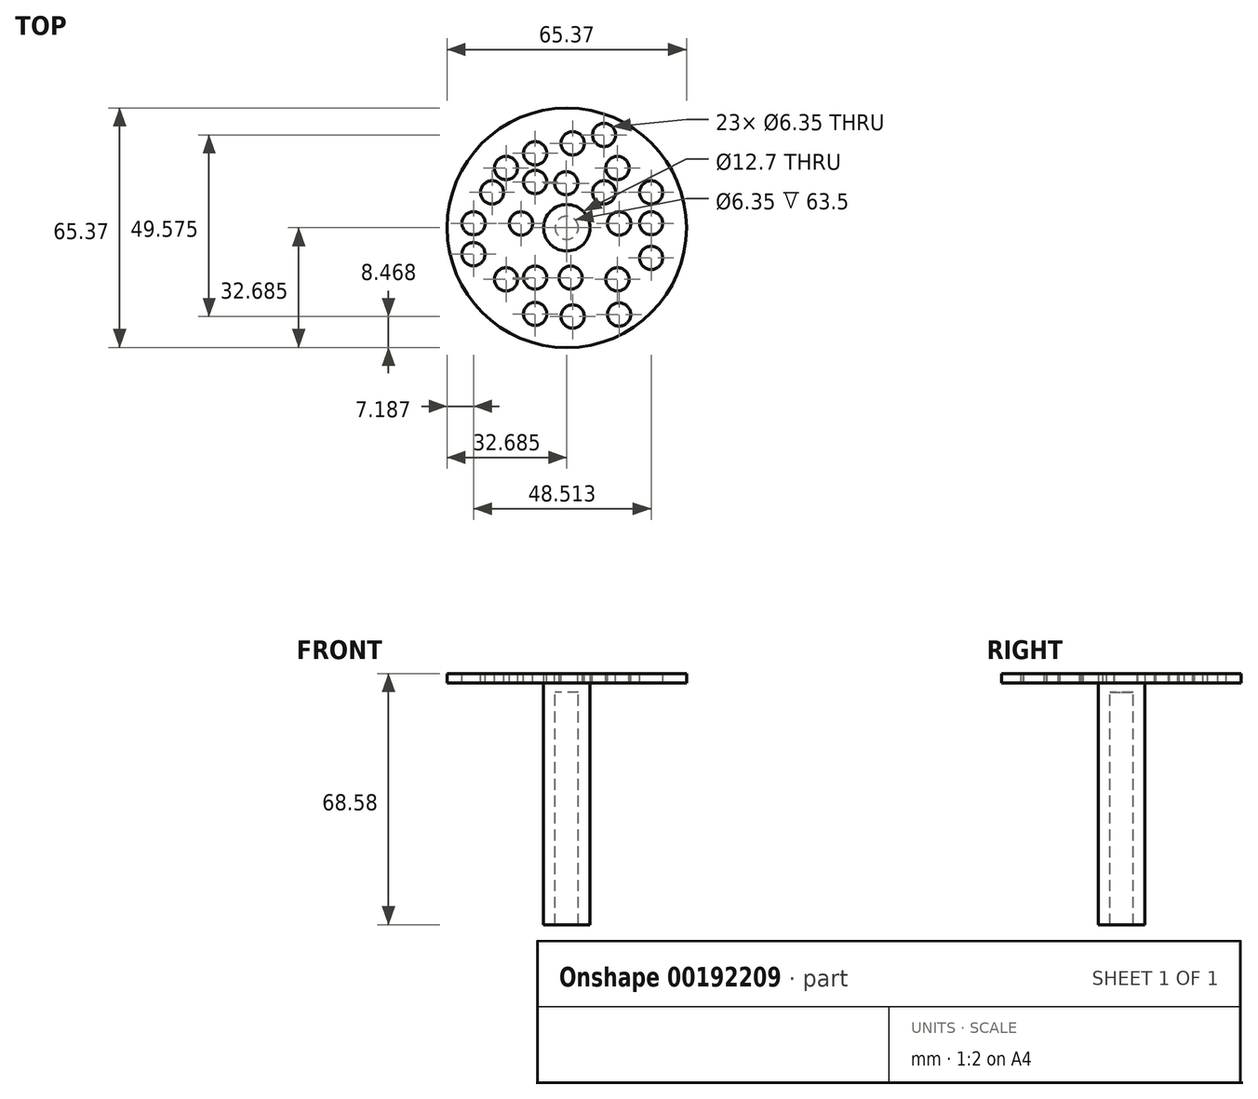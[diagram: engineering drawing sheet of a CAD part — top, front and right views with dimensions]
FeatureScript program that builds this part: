
annotation { "Feature Type Name" : "Feature", "Feature Type Description" : "" }
export const myFeature = defineFeature(function(context is Context, id is Id, definition is map)
    precondition{}
    {
        {
            var Q0;
            Q0=qCreatedBy(makeId("Top.planeOp"),FACE);
            var sketch = newSketch(context, id + "F0", { "sketchPlane" : qUnion([Q0])});
            skCircle(sketch, "E0", {"center": v(-23.02, -49.18) * mm, "radius": 6.35 * mm});
            skSolve(sketch);
        }
        {
            var Q0;
            Q0=makeQuery(id+"F0.imprint","IMPRINT",FACE,{"disambiguationData":[TD([[makeQuery(id+"F0.imprint","IMPRINT",EDGE,{"derivedFrom":sQuery(id+"F0.wireOp",EDGE,"E0")}),1.0]])]});
            extrude(context, id + "F1", {"entities" : qUnion([Q0]), "depth" : 63.5 * mm});
        }
        {
            var Q0;
            Q0=makeQuery(id+"F1.opExtrude","CAP_FACE",FACE,{"disambiguationData":[OSD([sQuery(id+"F0.wireOp",EDGE,"E0")])],"isStart":false});
            var sketch = newSketch(context, id + "F2", { "sketchPlane" : qUnion([Q0])});
            skCircle(sketch, "E1", {"center": v(-23.02, -49.18) * mm, "radius": 6.35 * mm});
            skSolve(sketch);
        }
        {
            var Q0;
            Q0=makeQuery(id+"F1.opExtrude","CAP_FACE",FACE,{"disambiguationData":[OSD([sQuery(id+"F0.wireOp",EDGE,"E0")])],"isStart":false});
            var sketch = newSketch(context, id + "F3", { "sketchPlane" : qUnion([Q0])});
            skSolve(sketch);
        }
        {
            var Q0;
            Q0=qSketchRegion(id+"F3",true);
            var Q1;
            Q1=makeQuery(id+"F3.imprint","IMPRINT",FACE,{"disambiguationData":[TD([[makeQuery(id+"F3.imprint","IMPRINT",EDGE,{"derivedFrom":makeQuery(id+"F1.opExtrude","CAP_EDGE",EDGE,{"disambiguationData":[OSD([sQuery(id+"F0.wireOp",EDGE,"E0")])],"isStart":false})}),1.0]])]});
            extrude(context, id + "F4", {"entities" : qUnion([Q0, Q1]), "operationType" : NewBodyOperationType.ADD, "depth" : 2.54 * mm});
        }
        {
            var Q0;
            Q0=sQuery(id+"F2.wireOp",VERTEX,"E1.center");
            var Q1;
            Q1=makeQuery(id+"F1.opExtrude","SWEPT_BODY",BODY,{"disambiguationData":[OSD([sQuery(id+"F0.wireOp",EDGE,"E0")])]});
            hole(context, id + "F5", {"style" : HoleStyle.SIMPLE, "endStyle" : HoleEndStyle.BLIND, "holeDiameter" : 6.35 * mm, "holeDepth" : 63.5 * mm, "startFromSketch" : true, "locations" : qUnion([Q0]), "scope" : qUnion([Q1])});
        }
        {
            var Q0;
            Q0=makeQuery(id+"F4.opExtrude","CAP_FACE",FACE,{"disambiguationData":[OSD([sQuery(id+"F0.wireOp",EDGE,"E0")])],"isStart":false});
            var sketch = newSketch(context, id + "F6", { "sketchPlane" : qUnion([Q0])});
            skCircle(sketch, "E2", {"center": v(-23.02, -49.18) * mm, "radius": 32.69 * mm});
            skSolve(sketch);
        }
        {
            var Q0;
            Q0=makeQuery(id+"F6.imprint","IMPRINT",FACE,{"disambiguationData":[TD([[makeQuery(id+"F6.imprint","IMPRINT",EDGE,{"derivedFrom":sQuery(id+"F6.wireOp",EDGE,"E2")}),1.0]])]});
            extrude(context, id + "F7", {"entities" : qUnion([Q0]), "depth" : 2.54 * mm});
        }
        {
            var Q0;
            Q0=makeQuery(id+"F4.opExtrude","CAP_FACE",FACE,{"disambiguationData":[OSD([sQuery(id+"F0.wireOp",EDGE,"E0")])],"isStart":false});
            extrude(context, id + "F8", {"entities" : qUnion([Q0]), "depth" : 2.54 * mm});
        }
        {
            var Q0;
            Q0=makeQuery(id+"F7.opExtrude","CAP_FACE",FACE,{"disambiguationData":[OSD([sQuery(id+"F0.wireOp",EDGE,"E0"),sQuery(id+"F6.wireOp",EDGE,"E2")])],"isStart":false});
            var sketch = newSketch(context, id + "F9", { "sketchPlane" : qUnion([Q0])});
            skPoint(sketch, "E3", {"position": v(-48.46, -47.92) * mm});
            skPoint(sketch, "E4", {"position": v(-21.42, -26.1) * mm});
            skPoint(sketch, "E5", {"position": v(0, -47.92) * mm});
            skPoint(sketch, "E6", {"position": v(-21.42, -73.4) * mm});
            skPoint(sketch, "E7", {"position": v(-39.62, -63.25) * mm});
            skPoint(sketch, "E8", {"position": v(-39.62, -32.84) * mm});
            skPoint(sketch, "E9", {"position": v(-9.17, -32.84) * mm});
            skPoint(sketch, "E10", {"position": v(-9.17, -63.25) * mm});
            skPoint(sketch, "E11", {"position": v(-35.52, -48) * mm});
            skPoint(sketch, "E12", {"position": v(-8.75, -48) * mm});
            skPoint(sketch, "E13", {"position": v(-23.18, -37) * mm});
            skPoint(sketch, "E14", {"position": v(-21.98, -62.77) * mm});
            skPoint(sketch, "E15", {"position": v(-31.65, -62.77) * mm});
            skPoint(sketch, "E16", {"position": v(-31.65, -28.84) * mm});
            skPoint(sketch, "E17", {"position": v(0, -39.5) * mm});
            skPoint(sketch, "E18", {"position": v(0, -57.38) * mm});
            skPoint(sketch, "E19", {"position": v(-8.75, -72.83) * mm});
            skPoint(sketch, "E20", {"position": v(-31.65, -72.68) * mm});
            skPoint(sketch, "E21", {"position": v(-48.51, -56.36) * mm});
            skPoint(sketch, "E22", {"position": v(-12.84, -23.82) * mm});
            skPoint(sketch, "E23", {"position": v(-43.44, -39.5) * mm});
            skPoint(sketch, "E24", {"position": v(-12.84, -39.5) * mm});
            skPoint(sketch, "E25", {"position": v(-31.65, -36.64) * mm});
            skSolve(sketch);
        }
        {
            var Q0;
            Q0=sQuery(id+"F9.wireOp",VERTEX,"E3");
            var Q1;
            Q1=sQuery(id+"F9.wireOp",VERTEX,"E8");
            var Q2;
            Q2=sQuery(id+"F9.wireOp",VERTEX,"E4");
            var Q3;
            Q3=sQuery(id+"F9.wireOp",VERTEX,"E9");
            var Q4;
            Q4=sQuery(id+"F9.wireOp",VERTEX,"E5");
            var Q5;
            Q5=sQuery(id+"F9.wireOp",VERTEX,"E10");
            var Q6;
            Q6=sQuery(id+"F9.wireOp",VERTEX,"E6");
            var Q7;
            Q7=sQuery(id+"F9.wireOp",VERTEX,"E7");
            var Q8;
            Q8=sQuery(id+"F9.wireOp",VERTEX,"E21");
            var Q9;
            Q9=sQuery(id+"F9.wireOp",VERTEX,"E11");
            var Q10;
            Q10=sQuery(id+"F9.wireOp",VERTEX,"E25");
            var Q11;
            Q11=sQuery(id+"F9.wireOp",VERTEX,"E23");
            var Q12;
            Q12=sQuery(id+"F9.wireOp",VERTEX,"E16");
            var Q13;
            Q13=sQuery(id+"F9.wireOp",VERTEX,"E13");
            var Q14;
            Q14=sQuery(id+"F9.wireOp",VERTEX,"E24");
            var Q15;
            Q15=sQuery(id+"F9.wireOp",VERTEX,"E22");
            var Q16;
            Q16=sQuery(id+"F9.wireOp",VERTEX,"E17");
            var Q17;
            Q17=sQuery(id+"F9.wireOp",VERTEX,"E12");
            var Q18;
            Q18=sQuery(id+"F9.wireOp",VERTEX,"E18");
            var Q19;
            Q19=sQuery(id+"F9.wireOp",VERTEX,"E19");
            var Q20;
            Q20=sQuery(id+"F9.wireOp",VERTEX,"E14");
            var Q21;
            Q21=sQuery(id+"F9.wireOp",VERTEX,"E15");
            var Q22;
            Q22=sQuery(id+"F9.wireOp",VERTEX,"E20");
            var Q23;
            Q23=makeQuery(id+"F7.opExtrude","SWEPT_BODY",BODY,{"disambiguationData":[OSD([sQuery(id+"F0.wireOp",EDGE,"E0"),sQuery(id+"F6.wireOp",EDGE,"E2")])]});
            hole(context, id + "F10", {"style" : HoleStyle.SIMPLE, "endStyle" : HoleEndStyle.BLIND, "holeDiameter" : 6.35 * mm, "holeDepth" : 63.5 * mm, "startFromSketch" : true, "locations" : qUnion([Q0, Q1, Q2, Q3, Q4, Q5, Q6, Q7, Q8, Q9, Q10, Q11, Q12, Q13, Q14, Q15, Q16, Q17, Q18, Q19, Q20, Q21, Q22]), "scope" : qUnion([Q23])});
        }
    });
